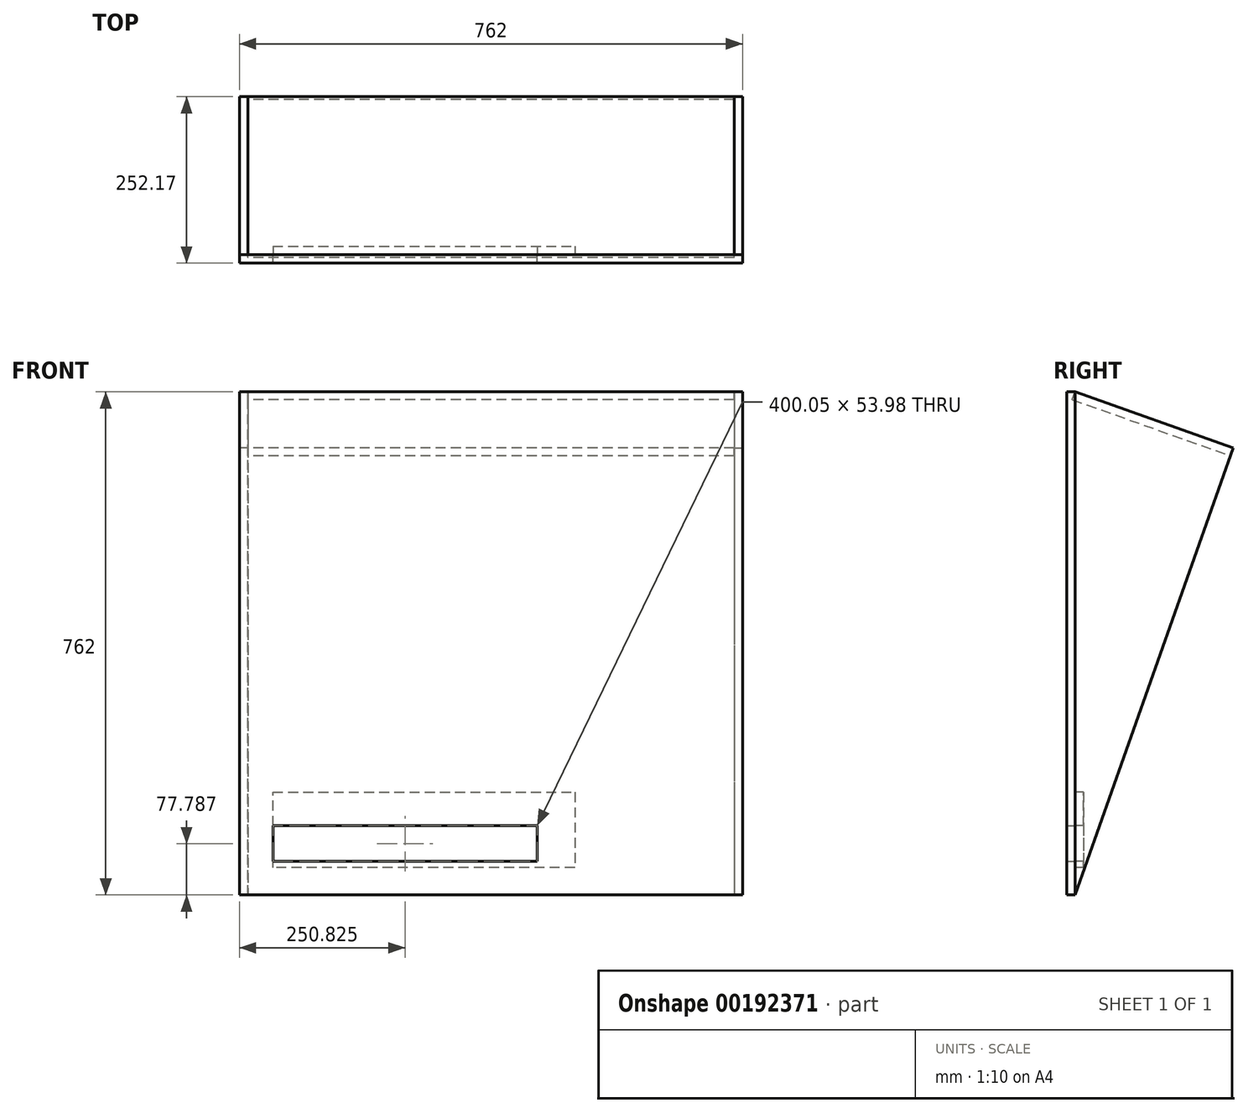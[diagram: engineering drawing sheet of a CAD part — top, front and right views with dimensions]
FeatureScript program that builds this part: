
annotation { "Feature Type Name" : "Feature", "Feature Type Description" : "" }
export const myFeature = defineFeature(function(context is Context, id is Id, definition is map)
    precondition{}
    {
        {
            var Q0;
            Q0=qCreatedBy(makeId("Front.planeOp"),FACE);
            var sketch = newSketch(context, id + "F0", { "sketchPlane" : qUnion([Q0])});
            skLineSegment(sketch, "E0", {"start": v(0, 0) * mm, "end": v(762, 0) * mm});
            skLineSegment(sketch, "E1", {"start": v(0, 0) * mm, "end": v(0, 762) * mm});
            skLineSegment(sketch, "E2", {"start": v(0, 762) * mm, "end": v(762, 762) * mm});
            skLineSegment(sketch, "E3", {"start": v(762, 762) * mm, "end": v(762, 0) * mm});
            skLineSegment(sketch, "E4", {"start": v(0, 0) * mm, "end": v(50.8, 0) * mm});
            skLineSegment(sketch, "E5", {"start": v(50.8, 0) * mm, "end": v(50.8, 50.8) * mm});
            skLineSegment(sketch, "E6", {"start": v(50.8, 50.8) * mm, "end": v(450.85, 50.8) * mm});
            skLineSegment(sketch, "E7", {"start": v(450.85, 50.8) * mm, "end": v(450.85, 104.77) * mm});
            skLineSegment(sketch, "E8", {"start": v(450.85, 104.77) * mm, "end": v(50.8, 104.77) * mm});
            skLineSegment(sketch, "E9", {"start": v(50.8, 104.77) * mm, "end": v(50.8, 50.8) * mm});
            skSolve(sketch);
        }
        {
            var Q0;
            Q0=makeQuery(id+"F0.imprint","IMPRINT",FACE,{"disambiguationData":[TD([[makeQuery(id+"F0.imprint","IMPRINT",EDGE,{"derivedFrom":sQuery(id+"F0.wireOp",EDGE,"E0")}),1.0]])]});
            extrude(context, id + "F1", {"entities" : qUnion([Q0]), "depth" : 6.35 * mm});
        }
        {
            var Q0;
            Q0=makeQuery(id+"F1.opExtrude","SWEPT_FACE",FACE,{"disambiguationData":[OSD([sQuery(id+"F0.wireOp",EDGE,"E3")])]});
            var sketch = newSketch(context, id + "F2", { "sketchPlane" : qUnion([Q0])});
            skSolve(sketch);
        }
        {
            var Q0;
            Q0 = qSketchRegion(id + "F2", true);
            var Q1;
            Q1=makeQuery(id+"F1.opExtrude","CAP_FACE",FACE,{"disambiguationData":[OSD([sQuery(id+"F0.wireOp",EDGE,"E0"),sQuery(id+"F0.wireOp",EDGE,"E1"),sQuery(id+"F0.wireOp",EDGE,"E2"),sQuery(id+"F0.wireOp",EDGE,"E3"),sQuery(id+"F0.wireOp",EDGE,"E4"),sQuery(id+"F0.wireOp",EDGE,"E6"),sQuery(id+"F0.wireOp",EDGE,"E7"),sQuery(id+"F0.wireOp",EDGE,"E8"),sQuery(id+"F0.wireOp",EDGE,"E9")])],"isStart":true});
            extrude(context, id + "F3", {"entities" : qUnion([Q0, Q1]), "operationType" : NewBodyOperationType.ADD, "depth" : 6.35 * mm});
        }
        {
            var Q0;
            Q0=makeQuery(id+"F3.opExtrude","CAP_FACE",FACE,{"disambiguationData":[OSD([sQuery(id+"F0.wireOp",EDGE,"E0"),sQuery(id+"F0.wireOp",EDGE,"E1"),sQuery(id+"F0.wireOp",EDGE,"E2"),sQuery(id+"F0.wireOp",EDGE,"E3"),sQuery(id+"F0.wireOp",EDGE,"E4"),sQuery(id+"F0.wireOp",EDGE,"E6"),sQuery(id+"F0.wireOp",EDGE,"E7"),sQuery(id+"F0.wireOp",EDGE,"E8"),sQuery(id+"F0.wireOp",EDGE,"E9")])],"isStart":false});
            var sketch = newSketch(context, id + "F4", { "sketchPlane" : qUnion([Q0])});
            skLineSegment(sketch, "E10", {"start": v(-50.8, 104.77) * mm, "end": v(-50.8, 155.57) * mm});
            skLineSegment(sketch, "E11", {"start": v(-50.8, 155.57) * mm, "end": v(-508, 155.57) * mm});
            skLineSegment(sketch, "E12", {"start": v(-508, 155.57) * mm, "end": v(-508, 41.27) * mm});
            skLineSegment(sketch, "E13", {"start": v(-508, 41.27) * mm, "end": v(-50.8, 41.27) * mm});
            skLineSegment(sketch, "E14", {"start": v(-50.8, 41.27) * mm, "end": v(-50.8, 104.77) * mm});
            skSolve(sketch);
        }
        {
            var Q0;
            {var subQ1=makeQuery(id+"F3.opExtrude","CAP_EDGE",EDGE,{"disambiguationData":[OSD([sQuery(id+"F0.wireOp",EDGE,"E6")])],"isStart":false});Q0=makeQuery(id+"F4.imprint","IMPRINT",FACE,{"disambiguationData":[TD([[makeQuery(id+"F4.imprint","IMPRINT",EDGE,{"derivedFrom":subQ1}),-1.0]])]});}
            extrude(context, id + "F5", {"entities" : qUnion([Q0]), "depth" : 12.7 * mm});
        }
        {
            var Q0;
            Q0=makeQuery(id+"F4.imprint","IMPRINT",FACE,{"disambiguationData":[TD([[makeQuery(id+"F4.imprint","IMPRINT",EDGE,{"derivedFrom":sQuery(id+"F4.wireOp",EDGE,"E10")}),1.0]])]});
            extrude(context, id + "F6", {"entities" : qUnion([Q0]), "depth" : 12.7 * mm});
        }
        {
            var Q0;
            {var subQ0=sQuery(id+"F0.wireOp",EDGE,"E3");Q0=makeQuery(id+"F3.boolean.opBoolean","MERGE",FACE,{"derivedFrom":[makeQuery(id+"F1.opExtrude","SWEPT_FACE",FACE,{"disambiguationData":[OSD([subQ0])]}),makeQuery(id+"F3.opExtrude","SWEPT_FACE",FACE,{"disambiguationData":[OSD([subQ0])]})]});}
            var sketch = newSketch(context, id + "F7", { "sketchPlane" : qUnion([Q0])});
            skLineSegment(sketch, "E15", {"start": v(6.35, 762) * mm, "end": v(245.82, 677.33) * mm});
            skLineSegment(sketch, "E16", {"start": v(245.82, 677.33) * mm, "end": v(6.35, 0) * mm});
            skSolve(sketch);
        }
        {
            var Q0;
            Q0 = qSketchRegion(id + "F7", true);
            var Q1;
            Q1=makeQuery(id+"F7.imprint","IMPRINT",FACE,{"disambiguationData":[TD([[makeQuery(id+"F7.imprint","IMPRINT",EDGE,{"derivedFrom":sQuery(id+"F7.wireOp",EDGE,"E15")}),-1.0]])]});
            extrude(context, id + "F8", {"entities" : qUnion([Q0, Q1]), "oppositeDirection" : true, "depth" : 12.7 * mm});
        }
        {
            var Q0;
            {var subQ0=sQuery(id+"F0.wireOp",EDGE,"E1");Q0=makeQuery(id+"F3.boolean.opBoolean","MERGE",FACE,{"derivedFrom":[makeQuery(id+"F1.opExtrude","SWEPT_FACE",FACE,{"disambiguationData":[OSD([subQ0])]}),makeQuery(id+"F3.opExtrude","SWEPT_FACE",FACE,{"disambiguationData":[OSD([subQ0])]})]});}
            var sketch = newSketch(context, id + "F9", { "sketchPlane" : qUnion([Q0])});
            skLineSegment(sketch, "E17.0.0", {"start": v(-6.35, 762) * mm, "end": v(-245.82, 677.33) * mm});
            skLineSegment(sketch, "E17.0.1", {"start": v(-245.82, 677.33) * mm, "end": v(-6.35, 0) * mm});
            skLineSegment(sketch, "E17.0.2", {"start": v(-6.35, 0) * mm, "end": v(-6.35, 762) * mm});
            skSolve(sketch);
        }
        {
            var Q0;
            Q0=makeQuery(id+"F9.imprint","IMPRINT",FACE,{"disambiguationData":[TD([[makeQuery(id+"F9.imprint","IMPRINT",EDGE,{"derivedFrom":sQuery(id+"F9.wireOp",EDGE,"E17.0.0")}),1.0]])]});
            extrude(context, id + "F10", {"entities" : qUnion([Q0]), "operationType" : NewBodyOperationType.ADD, "oppositeDirection" : true, "depth" : 12.7 * mm});
        }
        {
            var Q0;
            Q0=makeQuery(id+"F8.opExtrude","SWEPT_FACE",FACE,{"disambiguationData":[OSD([sQuery(id+"F7.wireOp",EDGE,"E15")])]});
            var sketch = newSketch(context, id + "F11", { "sketchPlane" : qUnion([Q0])});
            skLineSegment(sketch, "E18.0.0", {"start": v(0, 5.99) * mm, "end": v(0, -248.01) * mm});
            skLineSegment(sketch, "E18.0.1", {"start": v(0, -248.01) * mm, "end": v(12.7, -248.01) * mm});
            skLineSegment(sketch, "E18.0.2", {"start": v(12.7, -248.01) * mm, "end": v(12.7, 5.99) * mm});
            skLineSegment(sketch, "E18.0.3", {"start": v(12.7, 5.99) * mm, "end": v(0, 5.99) * mm});
            skLineSegment(sketch, "E19.bottom", {"start": v(749.3, 5.99) * mm, "end": v(12.7, 5.99) * mm});
            skLineSegment(sketch, "E19.top", {"start": v(749.3, -248.01) * mm, "end": v(12.7, -248.01) * mm});
            skLineSegment(sketch, "E19.left", {"start": v(749.3, 5.99) * mm, "end": v(749.3, -248.01) * mm});
            skLineSegment(sketch, "E19.right", {"start": v(12.7, 5.99) * mm, "end": v(12.7, -248.01) * mm});
            skSolve(sketch);
        }
        {
            var Q0;
            Q0=makeQuery(id+"F11.imprint","IMPRINT",FACE,{"disambiguationData":[TD([[makeQuery(id+"F11.imprint","IMPRINT",EDGE,{"derivedFrom":sQuery(id+"F11.wireOp",EDGE,"E19.bottom")}),1.0]])]});
            extrude(context, id + "F12", {"entities" : qUnion([Q0]), "oppositeDirection" : true, "depth" : 12.7 * mm});
        }
    });
